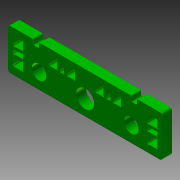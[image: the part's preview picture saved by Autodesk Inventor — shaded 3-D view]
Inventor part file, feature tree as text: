
AUTODESK INVENTOR PART (.ipt)
format: ipt  version: 2012 SP1 (Build 160190100, 190)  size: 257,536 bytes
history: native  units: in
note: dims shown in document units (in); Inventor stores cm internally (conversion verified against a paired STEP export)
features: other x3, extrude x1
ambient origin geometry x8: Origin, YZ Plane, XZ Plane, XY Plane, X Axis, Y Axis, Z Axis, Center Point
bodies: Solid1 (feature_tree)
feature tree (4):
  other  "skeleton.ipt"
  other  "STOCK_12MM"
  extrude  "Extrusion1"  Depth=0.3937in
  other  "THROUGH-CUT"
